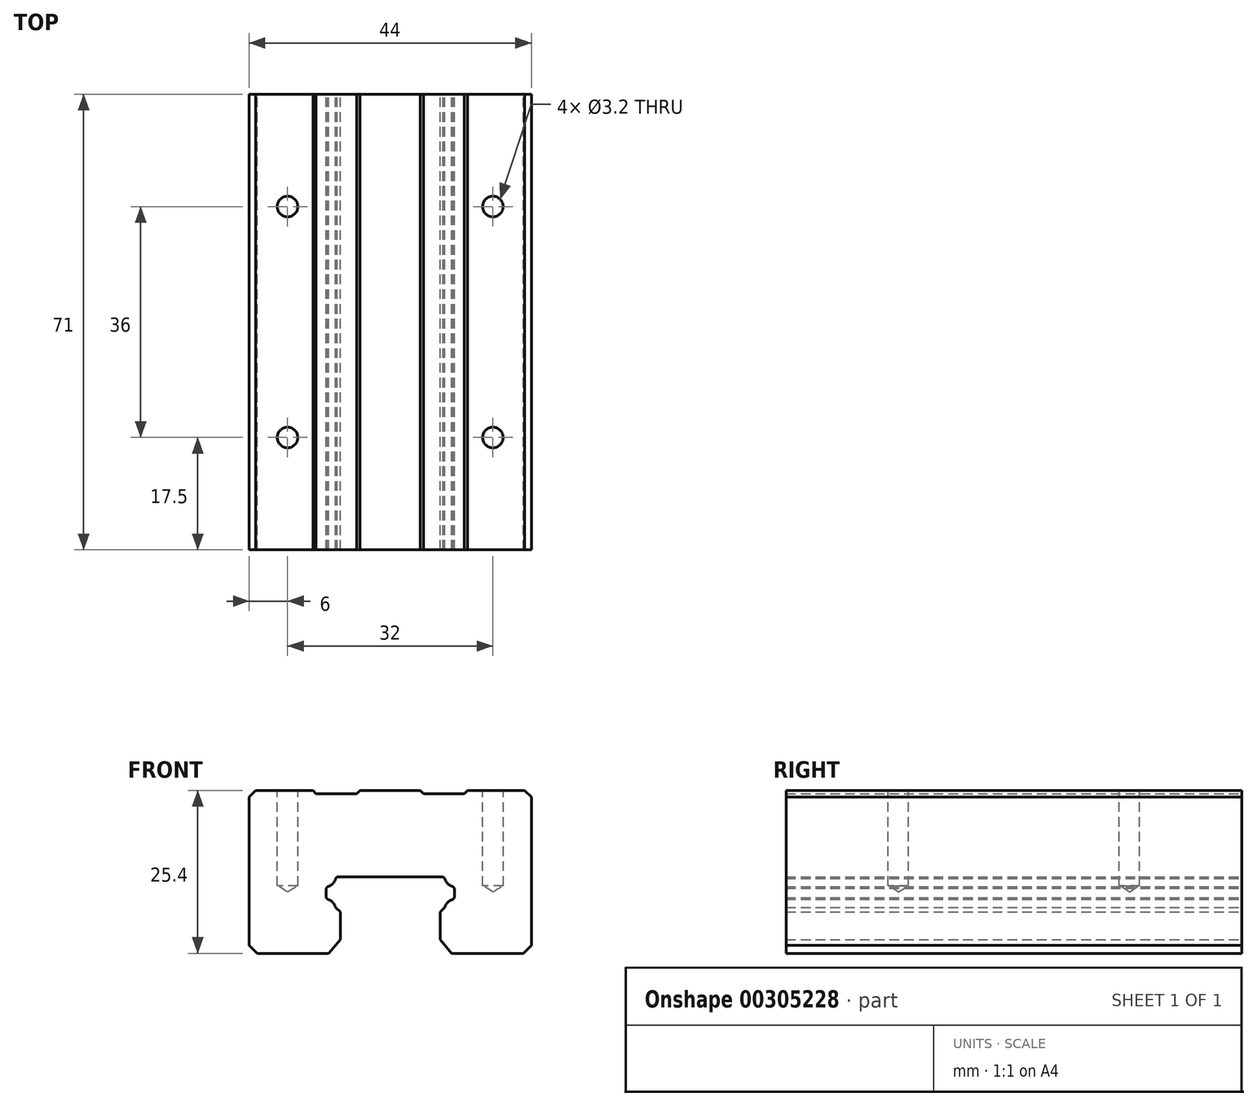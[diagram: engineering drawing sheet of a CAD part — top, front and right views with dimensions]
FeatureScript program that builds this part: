
annotation { "Feature Type Name" : "Feature", "Feature Type Description" : "" }
export const myFeature = defineFeature(function(context is Context, id is Id, definition is map)
    precondition{}
    {
        {
            var Q0;
            Q0=qCreatedBy(makeId("Front.planeOp"),FACE);
            var sketch = newSketch(context, id + "F0", { "sketchPlane" : qUnion([Q0])});
            skLineSegment(sketch, "E0.0.1", {"start": v(21.75, 0.73) * mm, "end": v(22, 0.98) * mm});
            skLineSegment(sketch, "E0.0.2", {"start": v(22, 0.98) * mm, "end": v(22, 9.63) * mm});
            skLineSegment(sketch, "E0.0.3", {"start": v(22, 9.63) * mm, "end": v(20.95, 10.68) * mm});
            skLineSegment(sketch, "E0.0.4", {"start": v(20.95, 10.68) * mm, "end": v(12.05, 10.68) * mm});
            skLineSegment(sketch, "E0.0.5", {"start": v(12.05, 10.68) * mm, "end": v(11.55, 10.18) * mm});
            skLineSegment(sketch, "E0.0.6", {"start": v(11.55, 10.18) * mm, "end": v(5.2, 10.18) * mm});
            skLineSegment(sketch, "E0.0.7", {"start": v(5.2, 10.18) * mm, "end": v(4.7, 10.68) * mm});
            skLineSegment(sketch, "E0.0.8", {"start": v(4.7, 10.68) * mm, "end": v(-4.7, 10.68) * mm});
            skLineSegment(sketch, "E0.0.9", {"start": v(-4.7, 10.68) * mm, "end": v(-5.2, 10.18) * mm});
            skLineSegment(sketch, "E0.0.10", {"start": v(-5.2, 10.18) * mm, "end": v(-11.55, 10.18) * mm});
            skLineSegment(sketch, "E0.0.11", {"start": v(-11.55, 10.18) * mm, "end": v(-12.05, 10.68) * mm});
            skLineSegment(sketch, "E0.0.12", {"start": v(-12.05, 10.68) * mm, "end": v(-20.95, 10.68) * mm});
            skLineSegment(sketch, "E0.0.13", {"start": v(-20.95, 10.68) * mm, "end": v(-22, 9.63) * mm});
            skLineSegment(sketch, "E0.0.14", {"start": v(-22, 9.63) * mm, "end": v(-22, 0.98) * mm});
            skLineSegment(sketch, "E1.0.0", {"start": v(-9.58, -14.72) * mm, "end": v(-7.8, -12.6) * mm});
            skLineSegment(sketch, "E1.0.1", {"start": v(-7.8, -12.6) * mm, "end": v(-7.8, -8.27) * mm});
            skLineSegment(sketch, "E1.0.2", {"start": v(-7.8, -8.27) * mm, "end": v(-8.5, -7.57) * mm});
            skArc(sketch, "E1.0.3", {"start": v(-8.5, -7.57) * mm, "mid": v(-8.96, -6.79) * mm, "end": v(-9.75, -6.33) * mm});
            skLineSegment(sketch, "E1.0.4", {"start": v(-9.75, -6.33) * mm, "end": v(-10, -6.07) * mm});
            skLineSegment(sketch, "E1.0.5", {"start": v(-10, -6.07) * mm, "end": v(-10, -4.57) * mm});
            skLineSegment(sketch, "E1.0.6", {"start": v(-10, -4.57) * mm, "end": v(-9.75, -4.32) * mm});
            skArc(sketch, "E1.0.7", {"start": v(-9.75, -4.32) * mm, "mid": v(-8.96, -3.86) * mm, "end": v(-8.5, -3.08) * mm});
            skLineSegment(sketch, "E1.0.8", {"start": v(-8.5, -3.08) * mm, "end": v(-8.25, -2.82) * mm});
            skLineSegment(sketch, "E1.0.9", {"start": v(-8.25, -2.82) * mm, "end": v(8.25, -2.82) * mm});
            skLineSegment(sketch, "E1.0.10", {"start": v(8.25, -2.82) * mm, "end": v(8.5, -3.08) * mm});
            skArc(sketch, "E1.0.11", {"start": v(8.5, -3.08) * mm, "mid": v(8.96, -3.86) * mm, "end": v(9.75, -4.32) * mm});
            skLineSegment(sketch, "E1.0.12", {"start": v(9.75, -4.32) * mm, "end": v(10, -4.57) * mm});
            skLineSegment(sketch, "E1.0.13", {"start": v(10, -4.57) * mm, "end": v(10, -6.07) * mm});
            skLineSegment(sketch, "E1.0.14", {"start": v(10, -6.07) * mm, "end": v(9.75, -6.33) * mm});
            skArc(sketch, "E1.0.15", {"start": v(9.75, -6.33) * mm, "mid": v(8.96, -6.79) * mm, "end": v(8.5, -7.57) * mm});
            skLineSegment(sketch, "E1.0.16", {"start": v(8.5, -7.57) * mm, "end": v(7.8, -8.27) * mm});
            skLineSegment(sketch, "E1.0.17", {"start": v(7.8, -8.27) * mm, "end": v(7.8, -12.6) * mm});
            skLineSegment(sketch, "E1.0.18", {"start": v(7.8, -12.6) * mm, "end": v(9.58, -14.72) * mm});
            skLineSegment(sketch, "E1.0.19", {"start": v(9.58, -14.72) * mm, "end": v(20.75, -14.72) * mm});
            skLineSegment(sketch, "E1.0.20", {"start": v(20.75, -14.72) * mm, "end": v(22, -13.47) * mm});
            skLineSegment(sketch, "E1.0.26", {"start": v(-22, -13.47) * mm, "end": v(-20.75, -14.72) * mm});
            skLineSegment(sketch, "E1.0.27", {"start": v(-20.75, -14.72) * mm, "end": v(-9.58, -14.72) * mm});
            skLineSegment(sketch, "E2", {"start": v(-22, 0.98) * mm, "end": v(-22, -13.47) * mm});
            skLineSegment(sketch, "E3", {"start": v(22, 0.98) * mm, "end": v(22, -13.47) * mm});
            skSolve(sketch);
        }
        {
            var Q0;
            Q0=makeQuery(id+"F0.imprint","IMPRINT",FACE,{"disambiguationData":[TD([[makeQuery(id+"F0.imprint","IMPRINT",EDGE,{"derivedFrom":sQuery(id+"F0.wireOp",EDGE,"E0.0.2")}),1.0]])]});
            extrude(context, id + "F1", {"entities" : qUnion([Q0]), "depth" : 71 * mm});
        }
        {
            var Q0;
            Q0=makeQuery(id+"F1.opExtrude","SWEPT_FACE",FACE,{"disambiguationData":[OSD([sQuery(id+"F0.wireOp",EDGE,"E0.0.12")])]});
            var sketch = newSketch(context, id + "F2", { "sketchPlane" : qUnion([Q0])});
            skPoint(sketch, "E4", {"position": v(-16, -17.5) * mm});
            skPoint(sketch, "E5", {"position": v(16, -17.5) * mm});
            skPoint(sketch, "E6", {"position": v(16, -53.5) * mm});
            skPoint(sketch, "E7", {"position": v(-16, -53.5) * mm});
            skSolve(sketch);
        }
        {
            var Q0;
            Q0=sQuery(id+"F2.wireOp",VERTEX,"E4");
            var Q1;
            Q1=sQuery(id+"F2.wireOp",VERTEX,"E7");
            var Q2;
            Q2=sQuery(id+"F2.wireOp",VERTEX,"E6");
            var Q3;
            Q3=sQuery(id+"F2.wireOp",VERTEX,"E5");
            var Q4;
            Q4=makeQuery(id+"F1.opExtrude","SWEPT_BODY",BODY,{"disambiguationData":[OSD([sQuery(id+"F0.wireOp",EDGE,"E0.0.2"),sQuery(id+"F0.wireOp",EDGE,"E0.0.3"),sQuery(id+"F0.wireOp",EDGE,"E0.0.4"),sQuery(id+"F0.wireOp",EDGE,"E0.0.5"),sQuery(id+"F0.wireOp",EDGE,"E0.0.6"),sQuery(id+"F0.wireOp",EDGE,"E0.0.7"),sQuery(id+"F0.wireOp",EDGE,"E0.0.8"),sQuery(id+"F0.wireOp",EDGE,"E0.0.9"),sQuery(id+"F0.wireOp",EDGE,"E0.0.10"),sQuery(id+"F0.wireOp",EDGE,"E0.0.11"),sQuery(id+"F0.wireOp",EDGE,"E0.0.12"),sQuery(id+"F0.wireOp",EDGE,"E0.0.13"),sQuery(id+"F0.wireOp",EDGE,"E0.0.14"),sQuery(id+"F0.wireOp",EDGE,"E1.0.0"),sQuery(id+"F0.wireOp",EDGE,"E1.0.1"),sQuery(id+"F0.wireOp",EDGE,"E1.0.2"),sQuery(id+"F0.wireOp",EDGE,"E1.0.3"),sQuery(id+"F0.wireOp",EDGE,"E1.0.4"),sQuery(id+"F0.wireOp",EDGE,"E1.0.5"),sQuery(id+"F0.wireOp",EDGE,"E1.0.6"),sQuery(id+"F0.wireOp",EDGE,"E1.0.7"),sQuery(id+"F0.wireOp",EDGE,"E1.0.8"),sQuery(id+"F0.wireOp",EDGE,"E1.0.9"),sQuery(id+"F0.wireOp",EDGE,"E1.0.10"),sQuery(id+"F0.wireOp",EDGE,"E1.0.11"),sQuery(id+"F0.wireOp",EDGE,"E1.0.12"),sQuery(id+"F0.wireOp",EDGE,"E1.0.13"),sQuery(id+"F0.wireOp",EDGE,"E1.0.14"),sQuery(id+"F0.wireOp",EDGE,"E1.0.15"),sQuery(id+"F0.wireOp",EDGE,"E1.0.16"),sQuery(id+"F0.wireOp",EDGE,"E1.0.17"),sQuery(id+"F0.wireOp",EDGE,"E1.0.18"),sQuery(id+"F0.wireOp",EDGE,"E1.0.19"),sQuery(id+"F0.wireOp",EDGE,"E1.0.20"),sQuery(id+"F0.wireOp",EDGE,"E1.0.26"),sQuery(id+"F0.wireOp",EDGE,"E1.0.27"),sQuery(id+"F0.wireOp",EDGE,"E2"),sQuery(id+"F0.wireOp",EDGE,"E3")])]});
            hole(context, id + "F3", {"style" : HoleStyle.SIMPLE, "endStyle" : HoleEndStyle.BLIND, "standardTappedOrClearance" : lookupTablePath({ "standard" : "ISO", "engagement" : "75%", "pitch" : "0.75 mm", "size" : "M4", "type" : "Tapped" }), "standardBlindInLast" : lookupTablePath({ "standard" : "ISO", "engagement" : "75%", "pitch" : "0.75 mm", "size" : "M4", "type" : "Tapped" }), "holeDiameter" : 3.2 * mm, "showTappedDepth" : true, "holeDepth" : 14.85 * mm, "tappedDepth" : 12.6 * mm, "tapClearance" : 3, "startFromSketch" : true, "locations" : qUnion([Q0, Q1, Q2, Q3]), "scope" : qUnion([Q4])});
        }
    });
